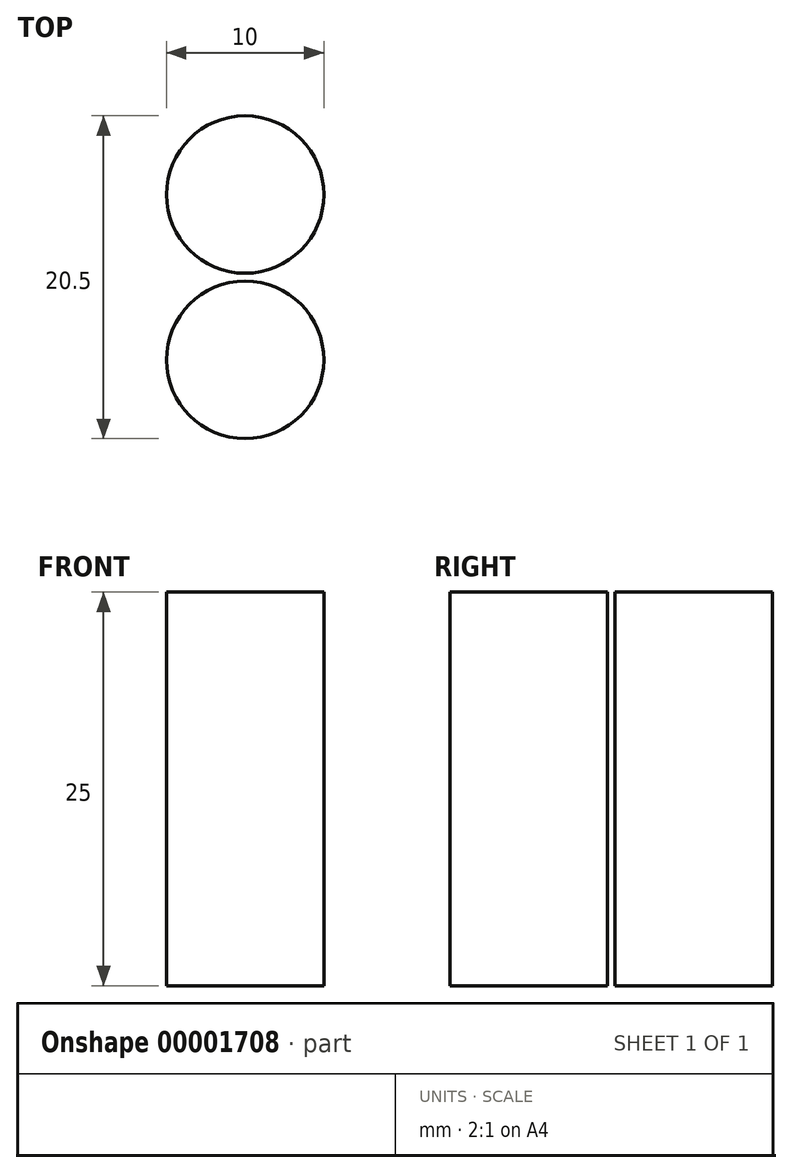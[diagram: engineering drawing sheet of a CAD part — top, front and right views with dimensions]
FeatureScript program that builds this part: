
annotation { "Feature Type Name" : "Feature", "Feature Type Description" : "" }
export const myFeature = defineFeature(function(context is Context, id is Id, definition is map)
    precondition{}
    {
        {
            var Q0;
            Q0=qCreatedBy(makeId("Top.planeOp"),FACE);
            var sketch = newSketch(context, id + "F0", { "sketchPlane" : qUnion([Q0])});
            skCircle(sketch, "E0", {"center": v(0, 10.5) * mm, "radius": 5 * mm});
            skCircle(sketch, "E1", {"center": v(0, 0) * mm, "radius": 5 * mm});
            skArc(sketch, "E2", {"start": v(-2.42, 4.38) * mm, "mid": v(-1.9, 5.25) * mm, "end": v(-2.42, 6.12) * mm});
            skArc(sketch, "E3", {"start": v(6.67, -32.2) * mm, "mid": v(10.06, -25.43) * mm, "end": v(2.88, -23.05) * mm});
            skArc(sketch, "E4", {"start": v(6.67, -32.2) * mm, "mid": v(5.92, -33.32) * mm, "end": v(6.98, -34.16) * mm});
            skArc(sketch, "E5", {"start": v(6.77, -44.12) * mm, "mid": v(12.33, -39.25) * mm, "end": v(6.98, -34.16) * mm});
            skSolve(sketch);
        }
        {
            var Q0;
            {Q0=qUnion([makeQuery(id+"F0.imprint","IMPRINT",FACE,{"disambiguationData":[TD([[makeQuery(id+"F0.imprint","IMPRINT",EDGE,{"derivedFrom":sQuery(id+"F0.wireOp",EDGE,"E0")}),1.0]])]}),makeQuery(id+"F0.imprint","IMPRINT",FACE,{"disambiguationData":[TD([[makeQuery(id+"F0.imprint","IMPRINT",EDGE,{"derivedFrom":sQuery(id+"F0.wireOp",EDGE,"E1")}),1.0]])]})]);}
            extrude(context, id + "F1", {"entities" : qUnion([Q0]), "depth" : 25 * mm});
        }
    });
